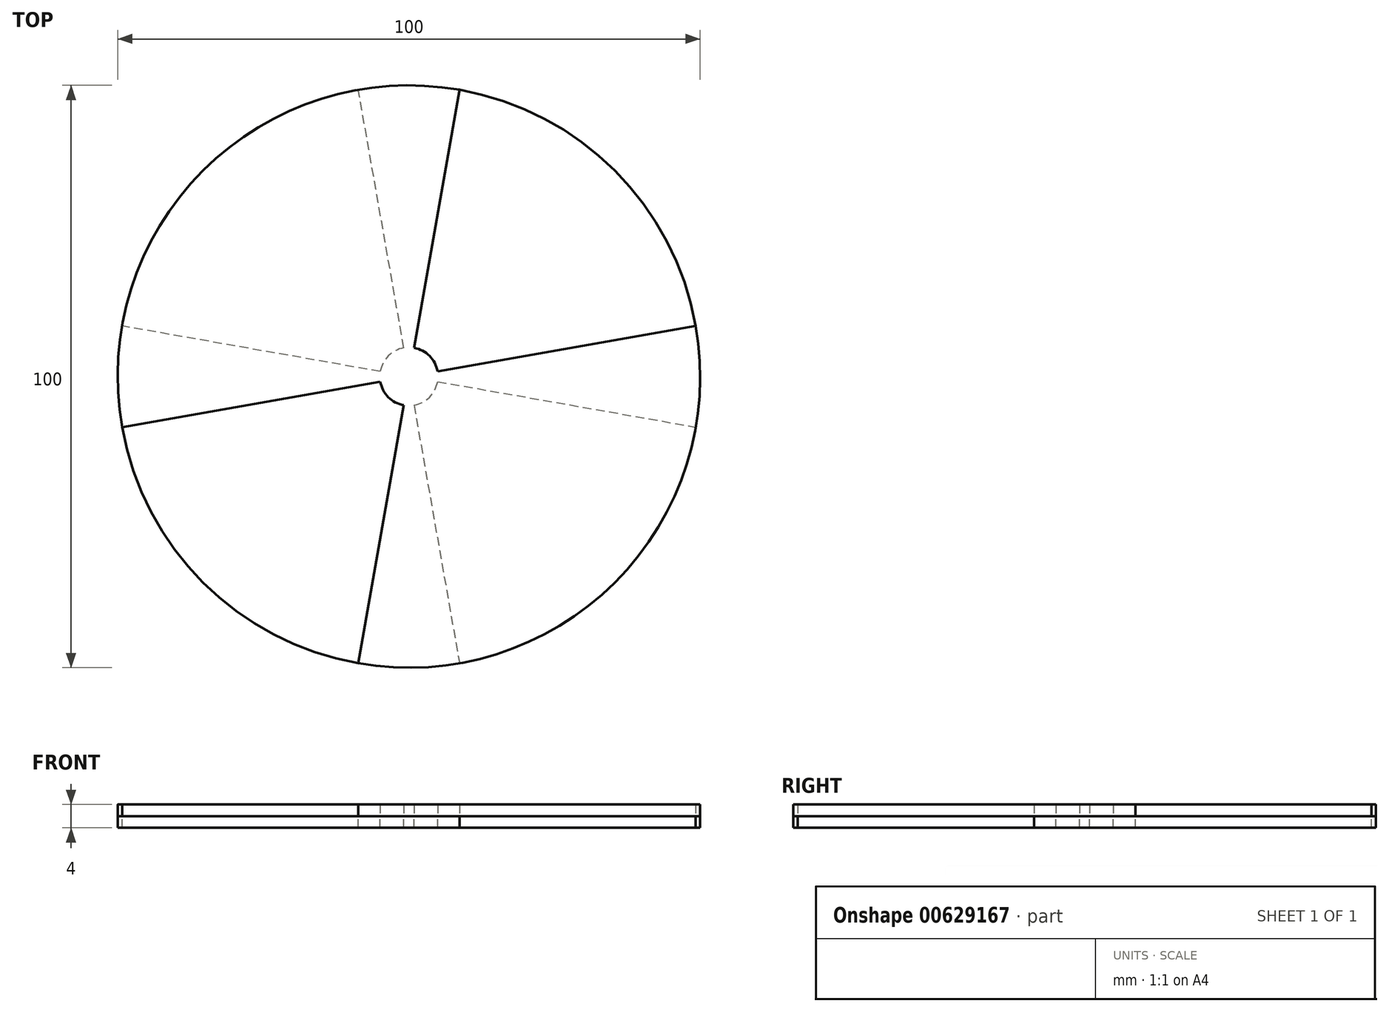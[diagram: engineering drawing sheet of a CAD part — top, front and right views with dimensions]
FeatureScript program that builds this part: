
annotation { "Feature Type Name" : "Feature", "Feature Type Description" : "" }
export const myFeature = defineFeature(function(context is Context, id is Id, definition is map)
    precondition{}
    {
        {
            var Q0;
            Q0=qCreatedBy(makeId("Top.planeOp"),FACE);
            var sketch = newSketch(context, id + "F0", { "sketchPlane" : qUnion([Q0])});
            skCircle(sketch, "E0", {"center": v(0, 0) * mm, "radius": 50 * mm});
            skLineSegment(sketch, "E1", {"start": v(0, 0) * mm, "end": v(0, 50) * mm});
            skCircle(sketch, "E2", {"center": v(0, 0) * mm, "radius": 5 * mm});
            skLineSegment(sketch, "E3", {"start": v(0, 0) * mm, "end": v(8.68, 49.24) * mm});
            skLineSegment(sketch, "E4", {"start": v(0, 0) * mm, "end": v(-8.68, 49.24) * mm});
            skLineSegment(sketch, "E5.1.0", {"start": v(0, 0) * mm, "end": v(-49.24, -8.68) * mm});
            skLineSegment(sketch, "E5.1.1", {"start": v(0, 0) * mm, "end": v(-50, 0) * mm});
            skLineSegment(sketch, "E5.1.2", {"start": v(0, 0) * mm, "end": v(-49.24, 8.68) * mm});
            skLineSegment(sketch, "E5.2.0", {"start": v(0, 0) * mm, "end": v(8.68, -49.24) * mm});
            skLineSegment(sketch, "E5.2.1", {"start": v(0, 0) * mm, "end": v(0, -50) * mm});
            skLineSegment(sketch, "E5.2.2", {"start": v(0, 0) * mm, "end": v(-8.68, -49.24) * mm});
            skLineSegment(sketch, "E5.3.0", {"start": v(0, 0) * mm, "end": v(49.24, 8.68) * mm});
            skLineSegment(sketch, "E5.3.1", {"start": v(0, 0) * mm, "end": v(50, 0) * mm});
            skLineSegment(sketch, "E5.3.2", {"start": v(0, 0) * mm, "end": v(49.24, -8.68) * mm});
            skSolve(sketch);
        }
        {
            var Q0;
            {var subQ0=sQuery(id+"F0.wireOp",EDGE,"E5.1.1");var subQ1=sQuery(id+"F0.wireOp",EDGE,"E0");var subQ2=makeQuery(id+"F0.imprint","INTERSECT",VERTEX,{"derivedFrom":[subQ1,subQ0]});Q0=makeQuery(id+"F0.imprint","IMPRINT",FACE,{"disambiguationData":[TD([[makeQuery(id+"F0.imprint","IMPRINT",EDGE,{"disambiguationData":[TD([[subQ2,1.0]])],"derivedFrom":subQ1}),1.0]])]});}
            var Q1;
            {var subQ0=sQuery(id+"F0.wireOp",EDGE,"E4");var subQ1=sQuery(id+"F0.wireOp",EDGE,"E0");var subQ2=makeQuery(id+"F0.imprint","INTERSECT",VERTEX,{"derivedFrom":[subQ1,subQ0]});Q1=makeQuery(id+"F0.imprint","IMPRINT",FACE,{"disambiguationData":[TD([[makeQuery(id+"F0.imprint","IMPRINT",EDGE,{"disambiguationData":[TD([[subQ2,-1.0]])],"derivedFrom":subQ1}),1.0]])]});}
            var Q2;
            {var subQ0=sQuery(id+"F0.wireOp",EDGE,"E1");var subQ1=sQuery(id+"F0.wireOp",EDGE,"E0");var subQ2=makeQuery(id+"F0.imprint","INTERSECT",VERTEX,{"derivedFrom":[subQ1,subQ0]});Q2=makeQuery(id+"F0.imprint","IMPRINT",FACE,{"disambiguationData":[TD([[makeQuery(id+"F0.imprint","IMPRINT",EDGE,{"disambiguationData":[TD([[subQ2,-1.0]])],"derivedFrom":subQ1}),1.0]])]});}
            var Q3;
            {var subQ0=sQuery(id+"F0.wireOp",EDGE,"E1");var subQ1=sQuery(id+"F0.wireOp",EDGE,"E0");var subQ2=makeQuery(id+"F0.imprint","INTERSECT",VERTEX,{"derivedFrom":[subQ1,subQ0]});Q3=makeQuery(id+"F0.imprint","IMPRINT",FACE,{"disambiguationData":[TD([[makeQuery(id+"F0.imprint","IMPRINT",EDGE,{"disambiguationData":[TD([[subQ2,1.0]])],"derivedFrom":subQ1}),1.0]])]});}
            var Q4;
            {var subQ0=sQuery(id+"F0.wireOp",EDGE,"E5.1.0");var subQ1=sQuery(id+"F0.wireOp",EDGE,"E0");var subQ2=makeQuery(id+"F0.imprint","INTERSECT",VERTEX,{"derivedFrom":[subQ1,subQ0]});Q4=makeQuery(id+"F0.imprint","IMPRINT",FACE,{"disambiguationData":[TD([[makeQuery(id+"F0.imprint","IMPRINT",EDGE,{"disambiguationData":[TD([[subQ2,1.0]])],"derivedFrom":subQ1}),1.0]])]});}
            var Q5;
            {var subQ0=sQuery(id+"F0.wireOp",EDGE,"E5.3.0");var subQ1=sQuery(id+"F0.wireOp",EDGE,"E0");var subQ2=makeQuery(id+"F0.imprint","INTERSECT",VERTEX,{"derivedFrom":[subQ1,subQ0]});Q5=makeQuery(id+"F0.imprint","IMPRINT",FACE,{"disambiguationData":[TD([[makeQuery(id+"F0.imprint","IMPRINT",EDGE,{"disambiguationData":[TD([[subQ2,1.0]])],"derivedFrom":subQ1}),1.0]])]});}
            var Q6;
            {var subQ0=sQuery(id+"F0.wireOp",EDGE,"E5.3.1");var subQ1=sQuery(id+"F0.wireOp",EDGE,"E0");var subQ2=makeQuery(id+"F0.imprint","INTERSECT",VERTEX,{"derivedFrom":[subQ1,subQ0]});Q6=makeQuery(id+"F0.imprint","IMPRINT",FACE,{"disambiguationData":[TD([[makeQuery(id+"F0.imprint","IMPRINT",EDGE,{"disambiguationData":[TD([[subQ2,1.0]])],"derivedFrom":subQ1}),1.0]])]});}
            var Q7;
            {var subQ0=sQuery(id+"F0.wireOp",EDGE,"E5.2.0");var subQ1=sQuery(id+"F0.wireOp",EDGE,"E0");var subQ2=makeQuery(id+"F0.imprint","INTERSECT",VERTEX,{"derivedFrom":[subQ1,subQ0]});Q7=makeQuery(id+"F0.imprint","IMPRINT",FACE,{"disambiguationData":[TD([[makeQuery(id+"F0.imprint","IMPRINT",EDGE,{"disambiguationData":[TD([[subQ2,-1.0]])],"derivedFrom":subQ1}),1.0]])]});}
            var Q8;
            {var subQ0=sQuery(id+"F0.wireOp",EDGE,"E5.2.0");var subQ1=sQuery(id+"F0.wireOp",EDGE,"E0");var subQ2=makeQuery(id+"F0.imprint","INTERSECT",VERTEX,{"derivedFrom":[subQ1,subQ0]});Q8=makeQuery(id+"F0.imprint","IMPRINT",FACE,{"disambiguationData":[TD([[makeQuery(id+"F0.imprint","IMPRINT",EDGE,{"disambiguationData":[TD([[subQ2,1.0]])],"derivedFrom":subQ1}),1.0]])]});}
            var Q9;
            {var subQ0=sQuery(id+"F0.wireOp",EDGE,"E5.2.1");var subQ1=sQuery(id+"F0.wireOp",EDGE,"E0");var subQ2=makeQuery(id+"F0.imprint","INTERSECT",VERTEX,{"derivedFrom":[subQ1,subQ0]});Q9=makeQuery(id+"F0.imprint","IMPRINT",FACE,{"disambiguationData":[TD([[makeQuery(id+"F0.imprint","IMPRINT",EDGE,{"disambiguationData":[TD([[subQ2,1.0]])],"derivedFrom":subQ1}),1.0]])]});}
            var Q10;
            {var subQ0=sQuery(id+"F0.wireOp",EDGE,"E5.1.1");var subQ1=sQuery(id+"F0.wireOp",EDGE,"E2");var subQ2=makeQuery(id+"F0.imprint","INTERSECT",VERTEX,{"derivedFrom":[subQ1,subQ0]});Q10=makeQuery(id+"F0.imprint","IMPRINT",FACE,{"disambiguationData":[TD([[makeQuery(id+"F0.imprint","IMPRINT",EDGE,{"disambiguationData":[TD([[subQ2,-1.0]])],"derivedFrom":subQ1}),1.0]])]});}
            var Q11;
            {var subQ0=sQuery(id+"F0.wireOp",EDGE,"E5.1.2");var subQ1=sQuery(id+"F0.wireOp",EDGE,"E2");var subQ2=makeQuery(id+"F0.imprint","INTERSECT",VERTEX,{"derivedFrom":[subQ1,subQ0]});Q11=makeQuery(id+"F0.imprint","IMPRINT",FACE,{"disambiguationData":[TD([[makeQuery(id+"F0.imprint","IMPRINT",EDGE,{"disambiguationData":[TD([[subQ2,-1.0]])],"derivedFrom":subQ1}),1.0]])]});}
            var Q12;
            {var subQ0=sQuery(id+"F0.wireOp",EDGE,"E4");var subQ1=sQuery(id+"F0.wireOp",EDGE,"E2");var subQ2=makeQuery(id+"F0.imprint","INTERSECT",VERTEX,{"derivedFrom":[subQ1,subQ0]});Q12=makeQuery(id+"F0.imprint","IMPRINT",FACE,{"disambiguationData":[TD([[makeQuery(id+"F0.imprint","IMPRINT",EDGE,{"disambiguationData":[TD([[subQ2,-1.0]])],"derivedFrom":subQ1}),1.0]])]});}
            var Q13;
            {var subQ1=sQuery(id+"F0.wireOp",EDGE,"E1");var subQ3=sQuery(id+"F0.wireOp",EDGE,"E2");var subQ4=makeQuery(id+"F0.imprint","INTERSECT",VERTEX,{"derivedFrom":[subQ1,subQ3]});Q13=makeQuery(id+"F0.imprint","IMPRINT",FACE,{"disambiguationData":[TD([[makeQuery(id+"F0.imprint","IMPRINT",EDGE,{"disambiguationData":[TD([[subQ4,-1.0]])],"derivedFrom":subQ3}),1.0]])]});}
            var Q14;
            {var subQ1=sQuery(id+"F0.wireOp",EDGE,"E1");var subQ3=sQuery(id+"F0.wireOp",EDGE,"E2");var subQ4=makeQuery(id+"F0.imprint","INTERSECT",VERTEX,{"derivedFrom":[subQ1,subQ3]});Q14=makeQuery(id+"F0.imprint","IMPRINT",FACE,{"disambiguationData":[TD([[makeQuery(id+"F0.imprint","IMPRINT",EDGE,{"disambiguationData":[TD([[subQ4,1.0]])],"derivedFrom":subQ3}),1.0]])]});}
            var Q15;
            {var subQ0=sQuery(id+"F0.wireOp",EDGE,"E5.3.0");var subQ1=sQuery(id+"F0.wireOp",EDGE,"E2");var subQ2=makeQuery(id+"F0.imprint","INTERSECT",VERTEX,{"derivedFrom":[subQ1,subQ0]});Q15=makeQuery(id+"F0.imprint","IMPRINT",FACE,{"disambiguationData":[TD([[makeQuery(id+"F0.imprint","IMPRINT",EDGE,{"disambiguationData":[TD([[subQ2,-1.0]])],"derivedFrom":subQ1}),1.0]])]});}
            var Q16;
            {var subQ0=sQuery(id+"F0.wireOp",EDGE,"E5.3.0");var subQ1=sQuery(id+"F0.wireOp",EDGE,"E2");var subQ2=makeQuery(id+"F0.imprint","INTERSECT",VERTEX,{"derivedFrom":[subQ1,subQ0]});Q16=makeQuery(id+"F0.imprint","IMPRINT",FACE,{"disambiguationData":[TD([[makeQuery(id+"F0.imprint","IMPRINT",EDGE,{"disambiguationData":[TD([[subQ2,1.0]])],"derivedFrom":subQ1}),1.0]])]});}
            var Q17;
            {var subQ0=sQuery(id+"F0.wireOp",EDGE,"E5.3.1");var subQ1=sQuery(id+"F0.wireOp",EDGE,"E2");var subQ2=makeQuery(id+"F0.imprint","INTERSECT",VERTEX,{"derivedFrom":[subQ1,subQ0]});Q17=makeQuery(id+"F0.imprint","IMPRINT",FACE,{"disambiguationData":[TD([[makeQuery(id+"F0.imprint","IMPRINT",EDGE,{"disambiguationData":[TD([[subQ2,1.0]])],"derivedFrom":subQ1}),1.0]])]});}
            var Q18;
            {var subQ0=sQuery(id+"F0.wireOp",EDGE,"E5.2.0");var subQ1=sQuery(id+"F0.wireOp",EDGE,"E2");var subQ2=makeQuery(id+"F0.imprint","INTERSECT",VERTEX,{"derivedFrom":[subQ1,subQ0]});Q18=makeQuery(id+"F0.imprint","IMPRINT",FACE,{"disambiguationData":[TD([[makeQuery(id+"F0.imprint","IMPRINT",EDGE,{"disambiguationData":[TD([[subQ2,-1.0]])],"derivedFrom":subQ1}),1.0]])]});}
            var Q19;
            {var subQ0=sQuery(id+"F0.wireOp",EDGE,"E5.2.1");var subQ1=sQuery(id+"F0.wireOp",EDGE,"E2");var subQ2=makeQuery(id+"F0.imprint","INTERSECT",VERTEX,{"derivedFrom":[subQ1,subQ0]});Q19=makeQuery(id+"F0.imprint","IMPRINT",FACE,{"disambiguationData":[TD([[makeQuery(id+"F0.imprint","IMPRINT",EDGE,{"disambiguationData":[TD([[subQ2,-1.0]])],"derivedFrom":subQ1}),1.0]])]});}
            var Q20;
            {var subQ0=sQuery(id+"F0.wireOp",EDGE,"E5.2.2");var subQ1=sQuery(id+"F0.wireOp",EDGE,"E2");var subQ2=makeQuery(id+"F0.imprint","INTERSECT",VERTEX,{"derivedFrom":[subQ1,subQ0]});Q20=makeQuery(id+"F0.imprint","IMPRINT",FACE,{"disambiguationData":[TD([[makeQuery(id+"F0.imprint","IMPRINT",EDGE,{"disambiguationData":[TD([[subQ2,-1.0]])],"derivedFrom":subQ1}),1.0]])]});}
            var Q21;
            {var subQ0=sQuery(id+"F0.wireOp",EDGE,"E5.1.0");var subQ1=sQuery(id+"F0.wireOp",EDGE,"E2");var subQ2=makeQuery(id+"F0.imprint","INTERSECT",VERTEX,{"derivedFrom":[subQ1,subQ0]});Q21=makeQuery(id+"F0.imprint","IMPRINT",FACE,{"disambiguationData":[TD([[makeQuery(id+"F0.imprint","IMPRINT",EDGE,{"disambiguationData":[TD([[subQ2,-1.0]])],"derivedFrom":subQ1}),1.0]])]});}
            extrude(context, id + "F1", {"entities" : qUnion([Q0, Q1, Q2, Q3, Q4, Q5, Q6, Q7, Q8, Q9, Q10, Q11, Q12, Q13, Q14, Q15, Q16, Q17, Q18, Q19, Q20, Q21]), "depth" : 2 * mm, "offsetDistance" : 25 * mm});
        }
        {
            var Q0;
            {var subQ0=sQuery(id+"F0.wireOp",EDGE,"E1");var subQ1=sQuery(id+"F0.wireOp",EDGE,"E0");var subQ2=makeQuery(id+"F0.imprint","INTERSECT",VERTEX,{"derivedFrom":[subQ1,subQ0]});Q0=makeQuery(id+"F0.imprint","IMPRINT",FACE,{"disambiguationData":[TD([[makeQuery(id+"F0.imprint","IMPRINT",EDGE,{"disambiguationData":[TD([[subQ2,1.0]])],"derivedFrom":subQ1}),1.0]])]});}
            var Q1;
            {var subQ0=sQuery(id+"F0.wireOp",EDGE,"E1");var subQ1=sQuery(id+"F0.wireOp",EDGE,"E0");var subQ2=makeQuery(id+"F0.imprint","INTERSECT",VERTEX,{"derivedFrom":[subQ1,subQ0]});Q1=makeQuery(id+"F0.imprint","IMPRINT",FACE,{"disambiguationData":[TD([[makeQuery(id+"F0.imprint","IMPRINT",EDGE,{"disambiguationData":[TD([[subQ2,-1.0]])],"derivedFrom":subQ1}),1.0]])]});}
            var Q2;
            {var subQ0=sQuery(id+"F0.wireOp",EDGE,"E3");var subQ1=sQuery(id+"F0.wireOp",EDGE,"E0");var subQ2=makeQuery(id+"F0.imprint","INTERSECT",VERTEX,{"derivedFrom":[subQ1,subQ0]});Q2=makeQuery(id+"F0.imprint","IMPRINT",FACE,{"disambiguationData":[TD([[makeQuery(id+"F0.imprint","IMPRINT",EDGE,{"disambiguationData":[TD([[subQ2,1.0]])],"derivedFrom":subQ1}),1.0]])]});}
            var Q3;
            {var subQ0=sQuery(id+"F0.wireOp",EDGE,"E5.3.0");var subQ1=sQuery(id+"F0.wireOp",EDGE,"E0");var subQ2=makeQuery(id+"F0.imprint","INTERSECT",VERTEX,{"derivedFrom":[subQ1,subQ0]});Q3=makeQuery(id+"F0.imprint","IMPRINT",FACE,{"disambiguationData":[TD([[makeQuery(id+"F0.imprint","IMPRINT",EDGE,{"disambiguationData":[TD([[subQ2,1.0]])],"derivedFrom":subQ1}),1.0]])]});}
            var Q4;
            {var subQ0=sQuery(id+"F0.wireOp",EDGE,"E5.3.1");var subQ1=sQuery(id+"F0.wireOp",EDGE,"E0");var subQ2=makeQuery(id+"F0.imprint","INTERSECT",VERTEX,{"derivedFrom":[subQ1,subQ0]});Q4=makeQuery(id+"F0.imprint","IMPRINT",FACE,{"disambiguationData":[TD([[makeQuery(id+"F0.imprint","IMPRINT",EDGE,{"disambiguationData":[TD([[subQ2,1.0]])],"derivedFrom":subQ1}),1.0]])]});}
            var Q5;
            {var subQ0=sQuery(id+"F0.wireOp",EDGE,"E5.1.1");var subQ1=sQuery(id+"F0.wireOp",EDGE,"E0");var subQ2=makeQuery(id+"F0.imprint","INTERSECT",VERTEX,{"derivedFrom":[subQ1,subQ0]});Q5=makeQuery(id+"F0.imprint","IMPRINT",FACE,{"disambiguationData":[TD([[makeQuery(id+"F0.imprint","IMPRINT",EDGE,{"disambiguationData":[TD([[subQ2,1.0]])],"derivedFrom":subQ1}),1.0]])]});}
            var Q6;
            {var subQ0=sQuery(id+"F0.wireOp",EDGE,"E5.1.0");var subQ1=sQuery(id+"F0.wireOp",EDGE,"E0");var subQ2=makeQuery(id+"F0.imprint","INTERSECT",VERTEX,{"derivedFrom":[subQ1,subQ0]});Q6=makeQuery(id+"F0.imprint","IMPRINT",FACE,{"disambiguationData":[TD([[makeQuery(id+"F0.imprint","IMPRINT",EDGE,{"disambiguationData":[TD([[subQ2,1.0]])],"derivedFrom":subQ1}),1.0]])]});}
            var Q7;
            {var subQ0=sQuery(id+"F0.wireOp",EDGE,"E5.1.0");var subQ1=sQuery(id+"F0.wireOp",EDGE,"E0");var subQ2=makeQuery(id+"F0.imprint","INTERSECT",VERTEX,{"derivedFrom":[subQ1,subQ0]});Q7=makeQuery(id+"F0.imprint","IMPRINT",FACE,{"disambiguationData":[TD([[makeQuery(id+"F0.imprint","IMPRINT",EDGE,{"disambiguationData":[TD([[subQ2,-1.0]])],"derivedFrom":subQ1}),1.0]])]});}
            var Q8;
            {var subQ0=sQuery(id+"F0.wireOp",EDGE,"E5.2.1");var subQ1=sQuery(id+"F0.wireOp",EDGE,"E0");var subQ2=makeQuery(id+"F0.imprint","INTERSECT",VERTEX,{"derivedFrom":[subQ1,subQ0]});Q8=makeQuery(id+"F0.imprint","IMPRINT",FACE,{"disambiguationData":[TD([[makeQuery(id+"F0.imprint","IMPRINT",EDGE,{"disambiguationData":[TD([[subQ2,1.0]])],"derivedFrom":subQ1}),1.0]])]});}
            var Q9;
            {var subQ0=sQuery(id+"F0.wireOp",EDGE,"E5.2.0");var subQ1=sQuery(id+"F0.wireOp",EDGE,"E0");var subQ2=makeQuery(id+"F0.imprint","INTERSECT",VERTEX,{"derivedFrom":[subQ1,subQ0]});Q9=makeQuery(id+"F0.imprint","IMPRINT",FACE,{"disambiguationData":[TD([[makeQuery(id+"F0.imprint","IMPRINT",EDGE,{"disambiguationData":[TD([[subQ2,1.0]])],"derivedFrom":subQ1}),1.0]])]});}
            var Q10;
            {var subQ0=sQuery(id+"F0.wireOp",EDGE,"E5.3.0");var subQ1=sQuery(id+"F0.wireOp",EDGE,"E2");var subQ2=makeQuery(id+"F0.imprint","INTERSECT",VERTEX,{"derivedFrom":[subQ1,subQ0]});Q10=makeQuery(id+"F0.imprint","IMPRINT",FACE,{"disambiguationData":[TD([[makeQuery(id+"F0.imprint","IMPRINT",EDGE,{"disambiguationData":[TD([[subQ2,-1.0]])],"derivedFrom":subQ1}),1.0]])]});}
            var Q11;
            {var subQ1=sQuery(id+"F0.wireOp",EDGE,"E1");var subQ3=sQuery(id+"F0.wireOp",EDGE,"E2");var subQ4=makeQuery(id+"F0.imprint","INTERSECT",VERTEX,{"derivedFrom":[subQ1,subQ3]});Q11=makeQuery(id+"F0.imprint","IMPRINT",FACE,{"disambiguationData":[TD([[makeQuery(id+"F0.imprint","IMPRINT",EDGE,{"disambiguationData":[TD([[subQ4,1.0]])],"derivedFrom":subQ3}),1.0]])]});}
            var Q12;
            {var subQ1=sQuery(id+"F0.wireOp",EDGE,"E1");var subQ3=sQuery(id+"F0.wireOp",EDGE,"E2");var subQ4=makeQuery(id+"F0.imprint","INTERSECT",VERTEX,{"derivedFrom":[subQ1,subQ3]});Q12=makeQuery(id+"F0.imprint","IMPRINT",FACE,{"disambiguationData":[TD([[makeQuery(id+"F0.imprint","IMPRINT",EDGE,{"disambiguationData":[TD([[subQ4,-1.0]])],"derivedFrom":subQ3}),1.0]])]});}
            var Q13;
            {var subQ0=sQuery(id+"F0.wireOp",EDGE,"E4");var subQ1=sQuery(id+"F0.wireOp",EDGE,"E2");var subQ2=makeQuery(id+"F0.imprint","INTERSECT",VERTEX,{"derivedFrom":[subQ1,subQ0]});Q13=makeQuery(id+"F0.imprint","IMPRINT",FACE,{"disambiguationData":[TD([[makeQuery(id+"F0.imprint","IMPRINT",EDGE,{"disambiguationData":[TD([[subQ2,-1.0]])],"derivedFrom":subQ1}),1.0]])]});}
            var Q14;
            {var subQ0=sQuery(id+"F0.wireOp",EDGE,"E5.1.2");var subQ1=sQuery(id+"F0.wireOp",EDGE,"E2");var subQ2=makeQuery(id+"F0.imprint","INTERSECT",VERTEX,{"derivedFrom":[subQ1,subQ0]});Q14=makeQuery(id+"F0.imprint","IMPRINT",FACE,{"disambiguationData":[TD([[makeQuery(id+"F0.imprint","IMPRINT",EDGE,{"disambiguationData":[TD([[subQ2,-1.0]])],"derivedFrom":subQ1}),1.0]])]});}
            var Q15;
            {var subQ0=sQuery(id+"F0.wireOp",EDGE,"E5.1.1");var subQ1=sQuery(id+"F0.wireOp",EDGE,"E2");var subQ2=makeQuery(id+"F0.imprint","INTERSECT",VERTEX,{"derivedFrom":[subQ1,subQ0]});Q15=makeQuery(id+"F0.imprint","IMPRINT",FACE,{"disambiguationData":[TD([[makeQuery(id+"F0.imprint","IMPRINT",EDGE,{"disambiguationData":[TD([[subQ2,-1.0]])],"derivedFrom":subQ1}),1.0]])]});}
            var Q16;
            {var subQ0=sQuery(id+"F0.wireOp",EDGE,"E5.1.0");var subQ1=sQuery(id+"F0.wireOp",EDGE,"E2");var subQ2=makeQuery(id+"F0.imprint","INTERSECT",VERTEX,{"derivedFrom":[subQ1,subQ0]});Q16=makeQuery(id+"F0.imprint","IMPRINT",FACE,{"disambiguationData":[TD([[makeQuery(id+"F0.imprint","IMPRINT",EDGE,{"disambiguationData":[TD([[subQ2,-1.0]])],"derivedFrom":subQ1}),1.0]])]});}
            var Q17;
            {var subQ0=sQuery(id+"F0.wireOp",EDGE,"E5.2.2");var subQ1=sQuery(id+"F0.wireOp",EDGE,"E2");var subQ2=makeQuery(id+"F0.imprint","INTERSECT",VERTEX,{"derivedFrom":[subQ1,subQ0]});Q17=makeQuery(id+"F0.imprint","IMPRINT",FACE,{"disambiguationData":[TD([[makeQuery(id+"F0.imprint","IMPRINT",EDGE,{"disambiguationData":[TD([[subQ2,-1.0]])],"derivedFrom":subQ1}),1.0]])]});}
            var Q18;
            {var subQ0=sQuery(id+"F0.wireOp",EDGE,"E5.2.1");var subQ1=sQuery(id+"F0.wireOp",EDGE,"E2");var subQ2=makeQuery(id+"F0.imprint","INTERSECT",VERTEX,{"derivedFrom":[subQ1,subQ0]});Q18=makeQuery(id+"F0.imprint","IMPRINT",FACE,{"disambiguationData":[TD([[makeQuery(id+"F0.imprint","IMPRINT",EDGE,{"disambiguationData":[TD([[subQ2,-1.0]])],"derivedFrom":subQ1}),1.0]])]});}
            var Q19;
            {var subQ0=sQuery(id+"F0.wireOp",EDGE,"E5.2.0");var subQ1=sQuery(id+"F0.wireOp",EDGE,"E2");var subQ2=makeQuery(id+"F0.imprint","INTERSECT",VERTEX,{"derivedFrom":[subQ1,subQ0]});Q19=makeQuery(id+"F0.imprint","IMPRINT",FACE,{"disambiguationData":[TD([[makeQuery(id+"F0.imprint","IMPRINT",EDGE,{"disambiguationData":[TD([[subQ2,-1.0]])],"derivedFrom":subQ1}),1.0]])]});}
            var Q20;
            {var subQ0=sQuery(id+"F0.wireOp",EDGE,"E5.3.0");var subQ1=sQuery(id+"F0.wireOp",EDGE,"E2");var subQ2=makeQuery(id+"F0.imprint","INTERSECT",VERTEX,{"derivedFrom":[subQ1,subQ0]});Q20=makeQuery(id+"F0.imprint","IMPRINT",FACE,{"disambiguationData":[TD([[makeQuery(id+"F0.imprint","IMPRINT",EDGE,{"disambiguationData":[TD([[subQ2,1.0]])],"derivedFrom":subQ1}),1.0]])]});}
            var Q21;
            {var subQ0=sQuery(id+"F0.wireOp",EDGE,"E5.3.1");var subQ1=sQuery(id+"F0.wireOp",EDGE,"E2");var subQ2=makeQuery(id+"F0.imprint","INTERSECT",VERTEX,{"derivedFrom":[subQ1,subQ0]});Q21=makeQuery(id+"F0.imprint","IMPRINT",FACE,{"disambiguationData":[TD([[makeQuery(id+"F0.imprint","IMPRINT",EDGE,{"disambiguationData":[TD([[subQ2,1.0]])],"derivedFrom":subQ1}),1.0]])]});}
            extrude(context, id + "F2", {"entities" : qUnion([Q0, Q1, Q2, Q3, Q4, Q5, Q6, Q7, Q8, Q9, Q10, Q11, Q12, Q13, Q14, Q15, Q16, Q17, Q18, Q19, Q20, Q21]), "oppositeDirection" : true, "depth" : 2 * mm, "offsetDistance" : 25 * mm});
        }
    });
